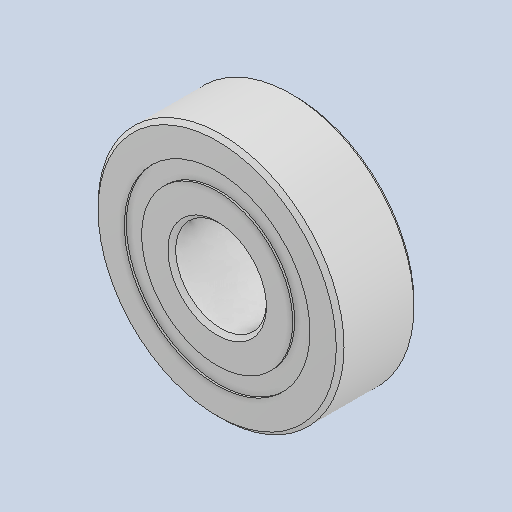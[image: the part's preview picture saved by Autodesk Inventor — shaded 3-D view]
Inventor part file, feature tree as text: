
AUTODESK INVENTOR PART (.ipt)
format: ipt  version: 2022 (Build 260153000, 153)  size: 599,040 bytes
history: mixed  units: mm
features: other x12, revolve x5, imported_body x1
ambient origin geometry x8: Origin, YZ Plane, XZ Plane, XY Plane, X Axis, Y Axis, Z Axis, Center Point
bodies: Solid1 (imported_parasolid), Solid2 (imported_parasolid), Solid3 (imported_parasolid), Solid4 (imported_parasolid), Solid5 (imported_parasolid), Solid6 (imported_parasolid), Solid7 (imported_parasolid), Solid8 (imported_parasolid), Solid9 (imported_parasolid), Solid10 (imported_parasolid), Solid11 (imported_parasolid), Solid12 (imported_parasolid), Solid13 (imported_parasolid), Solid14 (imported_parasolid), Solid15 (imported_parasolid), Solid16 (imported_parasolid), Solid17 (imported_parasolid)
feature tree (18):
  revolve  "Revolve1"  [1 undecoded]
  revolve  "Revolve2"  [1 undecoded]
  revolve  "Revolve3"  [1 undecoded]
  other  "CirPattern1[1]"
  other  "CirPattern1[2]"
  other  "CirPattern1[3]"
  other  "CirPattern1[4]"
  other  "CirPattern1[5]"
  other  "CirPattern1[6]"
  other  "CirPattern1[7]"
  other  "CirPattern1[8]"
  other  "CirPattern1[9]"
  other  "CirPattern1[10]"
  other  "CirPattern1[11]"
  other  "CirPattern1[12]"
  revolve  "Revolve5[1]"  [1 undecoded]
  revolve  "Revolve5[2]"  [1 undecoded]
  imported_body  NMx_Import_Brep_tag  [imported B-rep: ~37 faces, bbox_mm=[6.0, 0.0, 6.0]]
note: 5 required parameter values undecoded (feature->parameter linkage not recoverable at this tier; creation-order binding heuristic only, values carry confidence <= 0.55)
